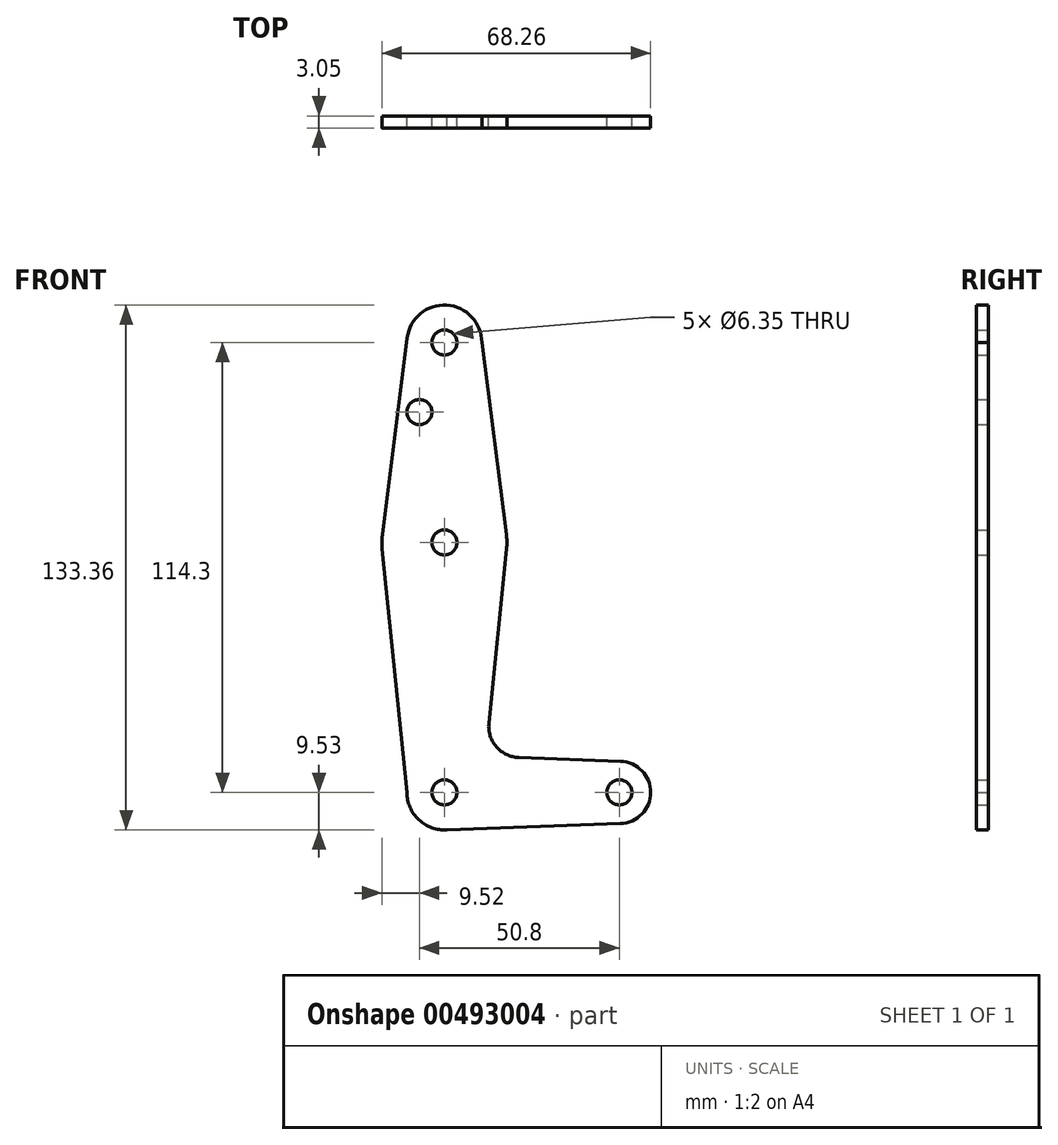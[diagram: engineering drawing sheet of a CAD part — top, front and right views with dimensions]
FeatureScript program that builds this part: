
annotation { "Feature Type Name" : "Feature", "Feature Type Description" : "" }
export const myFeature = defineFeature(function(context is Context, id is Id, definition is map)
    precondition{}
    {
        {
            var Q0;
            Q0=qCreatedBy(makeId("Front.planeOp"),FACE);
            var sketch = newSketch(context, id + "F0", { "sketchPlane" : qUnion([Q0])});
            skLineSegment(sketch, "E0", {"start": v(0, 0) * mm, "end": v(0, 114.3) * mm, "construction": true});
            skLineSegment(sketch, "E1", {"start": v(0, 0) * mm, "end": v(44.45, 0) * mm, "construction": true});
            skCircle(sketch, "E2", {"center": v(0, 114.3) * mm, "radius": 9.53 * mm});
            skCircle(sketch, "E3", {"center": v(0, 63.5) * mm, "radius": 15.88 * mm});
            skCircle(sketch, "E4", {"center": v(0, 0) * mm, "radius": 9.53 * mm});
            skCircle(sketch, "E5", {"center": v(44.45, 0) * mm, "radius": 7.94 * mm});
            skLineSegment(sketch, "E6", {"start": v(-9.45, 115.5) * mm, "end": v(-15.75, 65.48) * mm});
            skLineSegment(sketch, "E7", {"start": v(9.52, 114.3) * mm, "end": v(15.75, 65.5) * mm});
            skLineSegment(sketch, "E8", {"start": v(18.93, 8.85) * mm, "end": v(44.73, 7.93) * mm});
            skLineSegment(sketch, "E9", {"start": v(0, -9.53) * mm, "end": v(44.73, -7.93) * mm});
            skCircle(sketch, "E10", {"center": v(0, 114.3) * mm, "radius": 3.18 * mm});
            skCircle(sketch, "E11", {"center": v(0, 63.5) * mm, "radius": 3.18 * mm});
            skCircle(sketch, "E12", {"center": v(0, 0) * mm, "radius": 3.18 * mm});
            skCircle(sketch, "E13", {"center": v(44.45, 0) * mm, "radius": 3.18 * mm});
            skLineSegment(sketch, "E14", {"start": v(15.8, 61.9) * mm, "end": v(11.3, 17.6) * mm});
            skLineSegment(sketch, "E15", {"start": v(-15.8, 61.9) * mm, "end": v(-9.52, 0) * mm});
            skCircle(sketch, "E16", {"center": v(-6.35, 96.63) * mm, "radius": 3.18 * mm});
            skArc(sketch, "E17.filletArc", {"start": v(11.3, 17.6) * mm, "mid": v(13.22, 11.57) * mm, "end": v(18.93, 8.85) * mm});
            skSolve(sketch);
        }
        {
            var Q0;
            Q0 = qSketchRegion(id + "F0", true);
            extrude(context, id + "F1", {"entities" : qUnion([Q0]), "depth" : 3.05 * mm});
        }
    });
